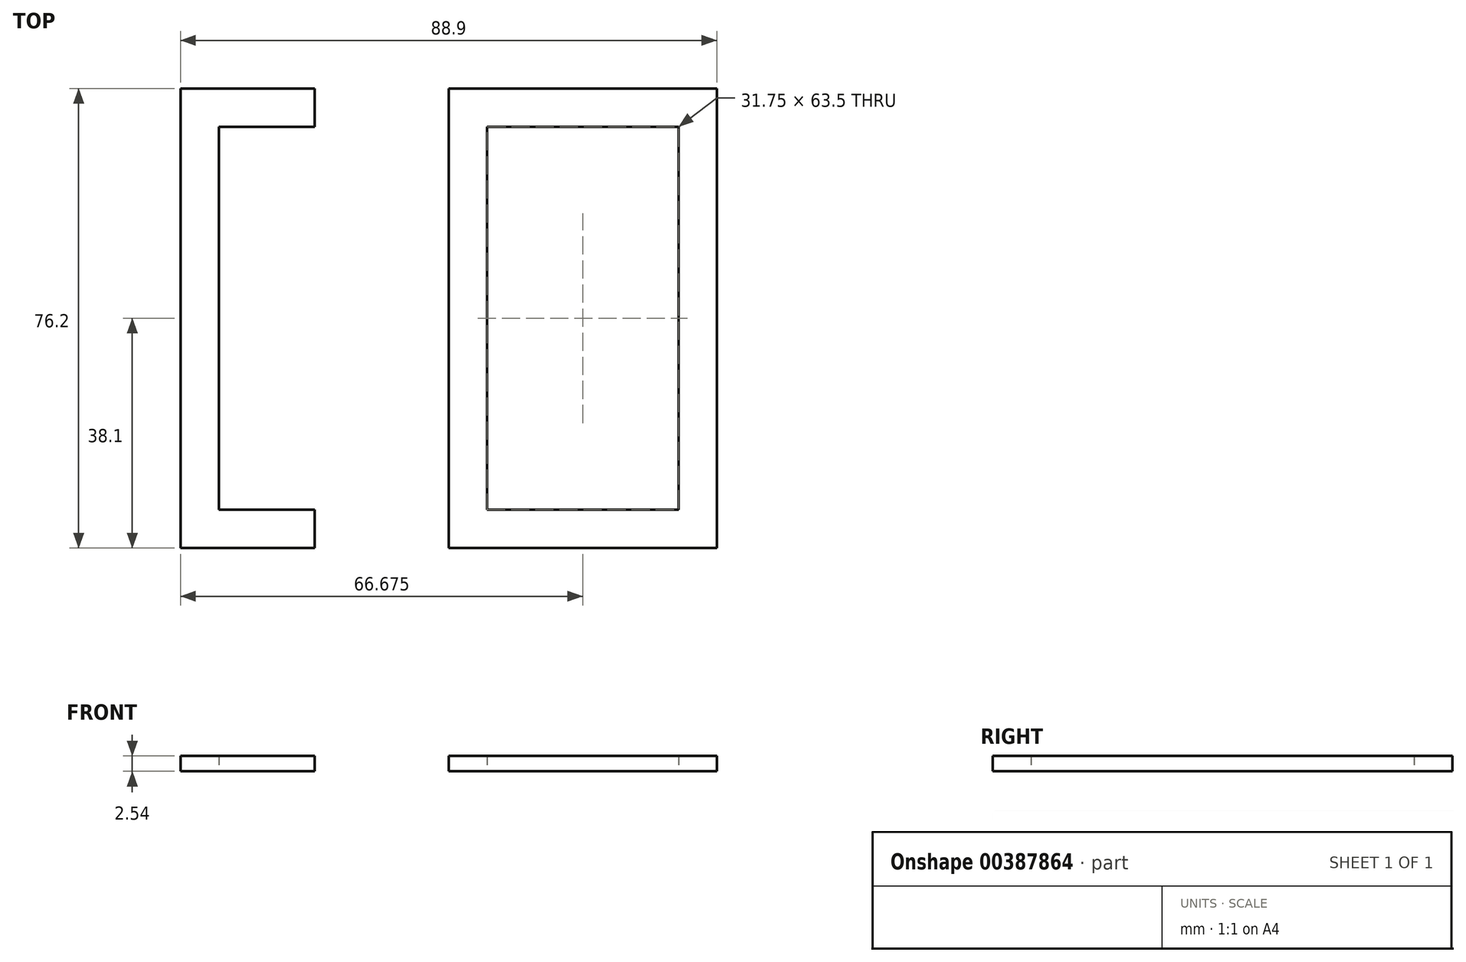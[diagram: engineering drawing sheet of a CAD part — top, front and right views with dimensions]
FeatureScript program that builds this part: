
annotation { "Feature Type Name" : "Feature", "Feature Type Description" : "" }
export const myFeature = defineFeature(function(context is Context, id is Id, definition is map)
    precondition{}
    {
        {
            var Q0;
            Q0=qCreatedBy(makeId("Top.planeOp"),FACE);
            var sketch = newSketch(context, id + "F0", { "sketchPlane" : qUnion([Q0])});
            skLineSegment(sketch, "E0.left", {"start": v(-44.45, 43.18) * mm, "end": v(-44.45, -33.02) * mm});
            skLineSegment(sketch, "E0.right", {"start": v(44.45, 43.18) * mm, "end": v(44.45, -33.02) * mm});
            skLineSegment(sketch, "E1", {"start": v(0, 0) * mm, "end": v(6.35, 0) * mm});
            skLineSegment(sketch, "E2", {"start": v(0, 0) * mm, "end": v(-6.35, 0) * mm});
            skLineSegment(sketch, "E3", {"start": v(-6.35, 0) * mm, "end": v(0, 0) * mm});
            skLineSegment(sketch, "E4", {"start": v(-44.45, 5.08) * mm, "end": v(-38.1, 5.08) * mm});
            skLineSegment(sketch, "E5", {"start": v(-44.45, 43.18) * mm, "end": v(0, 43.18) * mm});
            skLineSegment(sketch, "E6", {"start": v(44.45, 43.18) * mm, "end": v(0, 43.18) * mm});
            skLineSegment(sketch, "E7", {"start": v(-44.45, -33.02) * mm, "end": v(0, -33.02) * mm});
            skLineSegment(sketch, "E8", {"start": v(0, -33.02) * mm, "end": v(44.45, -33.02) * mm});
            skLineSegment(sketch, "E9", {"start": v(22.23, -33.02) * mm, "end": v(22.23, -26.67) * mm});
            skPoint(sketch, "E9.endSnap0", {"position": v(22.23, -33.02) * mm});
            skLineSegment(sketch, "E10", {"start": v(-22.23, -33.02) * mm, "end": v(-22.23, -26.67) * mm});
            skPoint(sketch, "E10.endSnap0", {"position": v(-22.23, -33.02) * mm});
            skPoint(sketch, "E11", {"position": v(-38.1, 36.83) * mm});
            skPoint(sketch, "E12", {"position": v(-38.1, -26.67) * mm});
            skPoint(sketch, "E13", {"position": v(38.1, -26.67) * mm});
            skPoint(sketch, "E14", {"position": v(38.1, 36.83) * mm});
            skLineSegment(sketch, "E15", {"start": v(-22.23, -26.67) * mm, "end": v(22.23, -26.67) * mm, "construction": true});
            skPoint(sketch, "E16", {"position": v(-6.35, -26.67) * mm});
            skPoint(sketch, "E17", {"position": v(6.35, -26.67) * mm});
            skLineSegment(sketch, "E18.bottom", {"start": v(-38.1, 36.83) * mm, "end": v(-6.35, 36.83) * mm});
            skLineSegment(sketch, "E18.top", {"start": v(-38.1, -26.67) * mm, "end": v(-6.35, -26.67) * mm});
            skLineSegment(sketch, "E18.left", {"start": v(-38.1, 36.83) * mm, "end": v(-38.1, -26.67) * mm});
            skLineSegment(sketch, "E18.right", {"start": v(-6.35, 36.83) * mm, "end": v(-6.35, -26.67) * mm});
            skLineSegment(sketch, "E19.bottom", {"start": v(6.35, -26.67) * mm, "end": v(38.1, -26.67) * mm});
            skLineSegment(sketch, "E19.top", {"start": v(6.35, 36.83) * mm, "end": v(38.1, 36.83) * mm});
            skLineSegment(sketch, "E19.left", {"start": v(6.35, -26.67) * mm, "end": v(6.35, 36.83) * mm});
            skLineSegment(sketch, "E19.right", {"start": v(38.1, -26.67) * mm, "end": v(38.1, 36.83) * mm});
            skLineSegment(sketch, "E20", {"start": v(0, 43.18) * mm, "end": v(0, -33.02) * mm});
            skLineSegment(sketch, "E21", {"start": v(44.45, 0) * mm, "end": v(38.1, 0) * mm});
            skLineSegment(sketch, "E22", {"start": v(-22.23, 43.18) * mm, "end": v(-22.23, 36.83) * mm});
            skLineSegment(sketch, "E23", {"start": v(22.23, 43.18) * mm, "end": v(22.22, 36.83) * mm});
            skSolve(sketch);
        }
        {
            var Q0;
            {var subQ4=sQuery(id+"F0.wireOp",EDGE,"E4");Q0=makeQuery(id+"F0.imprint","IMPRINT",FACE,{"disambiguationData":[TD([[makeQuery(id+"F0.imprint","IMPRINT",EDGE,{"derivedFrom":subQ4}),1.0]])]});}
            var Q1;
            {var subQ1=sQuery(id+"F0.wireOp",EDGE,"E3");Q1=makeQuery(id+"F0.imprint","IMPRINT",FACE,{"disambiguationData":[TD([[makeQuery(id+"F0.imprint","IMPRINT",EDGE,{"derivedFrom":subQ1}),1.0]])]});}
            var Q2;
            {var subQ1=sQuery(id+"F0.wireOp",EDGE,"E3");Q2=makeQuery(id+"F0.imprint","IMPRINT",FACE,{"disambiguationData":[TD([[makeQuery(id+"F0.imprint","IMPRINT",EDGE,{"derivedFrom":subQ1}),-1.0]])]});}
            var Q3;
            {var subQ5=sQuery(id+"F0.wireOp",EDGE,"E4");Q3=makeQuery(id+"F0.imprint","IMPRINT",FACE,{"disambiguationData":[TD([[makeQuery(id+"F0.imprint","IMPRINT",EDGE,{"derivedFrom":subQ5}),-1.0]])]});}
            var Q4;
            {var subQ4=sQuery(id+"F0.wireOp",EDGE,"E1");Q4=makeQuery(id+"F0.imprint","IMPRINT",FACE,{"disambiguationData":[TD([[makeQuery(id+"F0.imprint","IMPRINT",EDGE,{"derivedFrom":subQ4}),-1.0]])]});}
            var Q5;
            {var subQ4=sQuery(id+"F0.wireOp",EDGE,"E1");Q5=makeQuery(id+"F0.imprint","IMPRINT",FACE,{"disambiguationData":[TD([[makeQuery(id+"F0.imprint","IMPRINT",EDGE,{"derivedFrom":subQ4}),1.0]])]});}
            var Q6;
            {var subQ7=sQuery(id+"F0.wireOp",EDGE,"E21");Q6=makeQuery(id+"F0.imprint","IMPRINT",FACE,{"disambiguationData":[TD([[makeQuery(id+"F0.imprint","IMPRINT",EDGE,{"derivedFrom":subQ7}),-1.0]])]});}
            var Q7;
            {var subQ1=sQuery(id+"F0.wireOp",EDGE,"E9");Q7=makeQuery(id+"F0.imprint","IMPRINT",FACE,{"disambiguationData":[TD([[makeQuery(id+"F0.imprint","IMPRINT",EDGE,{"derivedFrom":subQ1}),-1.0]])]});}
            extrude(context, id + "F1", {"entities" : qUnion([Q0, Q1, Q2, Q3, Q4, Q5, Q6, Q7]), "depth" : 2.54 * mm});
        }
    });
